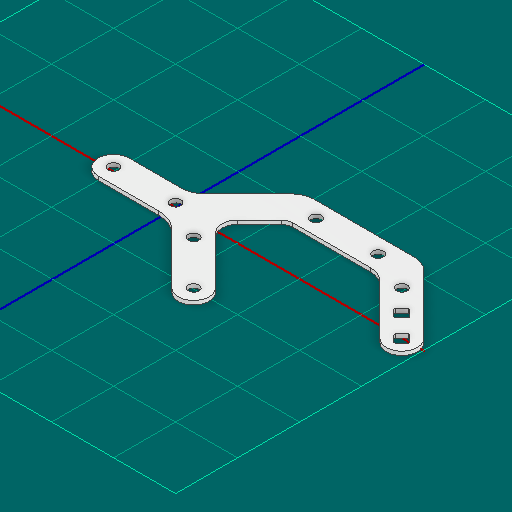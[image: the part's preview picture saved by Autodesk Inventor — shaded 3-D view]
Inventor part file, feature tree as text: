
AUTODESK INVENTOR PART (.ipt)
format: ipt  version: 2025 (Build 290162000, 162)  size: 202,752 bytes
history: native  units: in
note: dims shown in document units (in); Inventor stores cm internally (conversion verified against a paired STEP export)
features: other x6, sketch x1
ambient origin geometry x8: Origin, YZ Plane, XZ Plane, XY Plane, X Axis, Y Axis, Z Axis, Center Point
bodies: Solid1 (feature_tree)
feature tree (7):
  other  "join_gusset.ipt"
  other  "Blocks"
  other  "main"
  other  "Solid1::join_gusset.ipt"
  other  "TaggingFeature1"
  sketch  "Sketch1"  dims[d0=0.3937in d5=0.5in d6=135.0deg d7=0.375in d8=0.5in d9=0.375in d10=0.375in d11=0.5in d12=0.1875in d15=1.25in d16=0.5in d17=45.0deg d18=0.25in d19=0.172in d20=0.25in d24=0.172in]
  other  "main:1"
